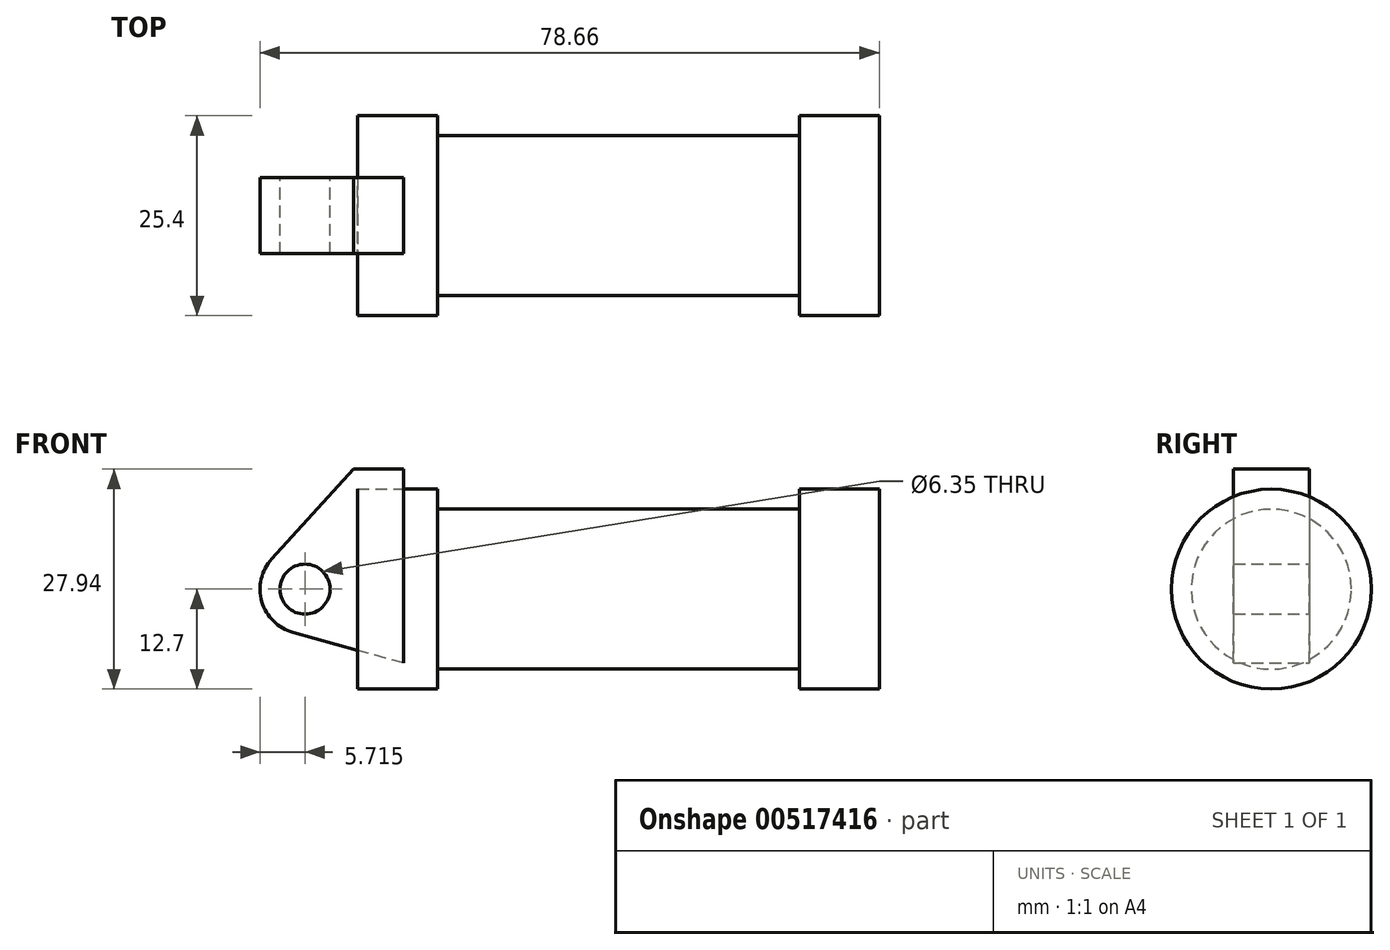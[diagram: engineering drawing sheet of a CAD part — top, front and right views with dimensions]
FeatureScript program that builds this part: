
annotation { "Feature Type Name" : "Feature", "Feature Type Description" : "" }
export const myFeature = defineFeature(function(context is Context, id is Id, definition is map)
    precondition{}
    {
        {
            var Q0;
            Q0=qCreatedBy(makeId("Front.planeOp"),FACE);
            var sketch = newSketch(context, id + "F0", { "sketchPlane" : qUnion([Q0])});
            skLineSegment(sketch, "E0", {"start": v(0, 0) * mm, "end": v(0, 12.7) * mm});
            skLineSegment(sketch, "E1", {"start": v(0, 12.7) * mm, "end": v(10.16, 12.7) * mm});
            skLineSegment(sketch, "E2", {"start": v(10.16, 12.7) * mm, "end": v(10.16, 10.16) * mm});
            skLineSegment(sketch, "E3", {"start": v(10.16, 10.16) * mm, "end": v(56.13, 10.16) * mm});
            skLineSegment(sketch, "E4", {"start": v(56.13, 10.16) * mm, "end": v(56.13, 12.7) * mm});
            skLineSegment(sketch, "E5", {"start": v(56.13, 12.7) * mm, "end": v(66.3, 12.7) * mm});
            skLineSegment(sketch, "E6", {"start": v(66.3, 12.7) * mm, "end": v(66.3, 0) * mm});
            skLineSegment(sketch, "E7", {"start": v(66.3, 0) * mm, "end": v(0, 0) * mm});
            skLineSegment(sketch, "E8", {"start": v(5.84, 15.24) * mm, "end": v(-0.5, 15.24) * mm});
            skLineSegment(sketch, "E9", {"start": v(-0.5, 15.24) * mm, "end": v(-10.88, 3.85) * mm});
            skLineSegment(sketch, "E10", {"start": v(0, 0) * mm, "end": v(-6.65, 0) * mm});
            skCircle(sketch, "E11", {"center": v(-6.65, 0) * mm, "radius": 5.72 * mm});
            skCircle(sketch, "E12", {"center": v(-6.65, 0) * mm, "radius": 3.18 * mm});
            skLineSegment(sketch, "E13", {"start": v(5.84, 15.24) * mm, "end": v(5.84, -9.4) * mm});
            skLineSegment(sketch, "E14", {"start": v(5.84, -9.4) * mm, "end": v(-8.18, -5.5) * mm});
            skSolve(sketch);
        }
        {
            var Q0;
            {var subQ0=sQuery(id+"F0.wireOp",EDGE,"E2");Q0=makeQuery(id+"F0.imprint","IMPRINT",FACE,{"disambiguationData":[TD([[makeQuery(id+"F0.imprint","IMPRINT",EDGE,{"derivedFrom":subQ0}),-1.0]])]});}
            var Q1;
            {var subQ0=sQuery(id+"F0.wireOp",EDGE,"E0");Q1=makeQuery(id+"F0.imprint","IMPRINT",FACE,{"disambiguationData":[TD([[makeQuery(id+"F0.imprint","IMPRINT",EDGE,{"derivedFrom":subQ0}),-1.0]])]});}
            var Q2;
            Q2=sQuery(id+"F0.wireOp",EDGE,"E7");
            revolve(context, id + "F1", {"entities" : qUnion([Q0, Q1]), "axis" : qUnion([Q2]), "revolveType" : RevolveType.FULL});
        }
        {
            var Q0;
            {var subQ1=sQuery(id+"F0.wireOp",EDGE,"E0");Q0=makeQuery(id+"F0.imprint","IMPRINT",FACE,{"disambiguationData":[TD([[makeQuery(id+"F0.imprint","IMPRINT",EDGE,{"derivedFrom":subQ1}),1.0]])]});}
            var Q1;
            {var subQ5=sQuery(id+"F0.wireOp",EDGE,"E12");Q1=makeQuery(id+"F0.imprint","IMPRINT",FACE,{"disambiguationData":[TD([[makeQuery(id+"F0.imprint","IMPRINT",EDGE,{"derivedFrom":subQ5}),-1.0]])]});}
            var Q2;
            {var subQ0=sQuery(id+"F0.wireOp",EDGE,"E14");Q2=makeQuery(id+"F0.imprint","IMPRINT",FACE,{"disambiguationData":[TD([[makeQuery(id+"F0.imprint","IMPRINT",EDGE,{"derivedFrom":subQ0}),-1.0]])]});}
            var Q3;
            {var subQ0=sQuery(id+"F0.wireOp",EDGE,"E0");Q3=makeQuery(id+"F0.imprint","IMPRINT",FACE,{"disambiguationData":[TD([[makeQuery(id+"F0.imprint","IMPRINT",EDGE,{"derivedFrom":subQ0}),-1.0]])]});}
            extrude(context, id + "F2", {"entities" : qUnion([Q0, Q1, Q2, Q3]), "endBound" : BoundingType.SYMMETRIC, "depth" : 9.65 * mm, "offsetDistance" : 25.4 * mm});
        }
    });
